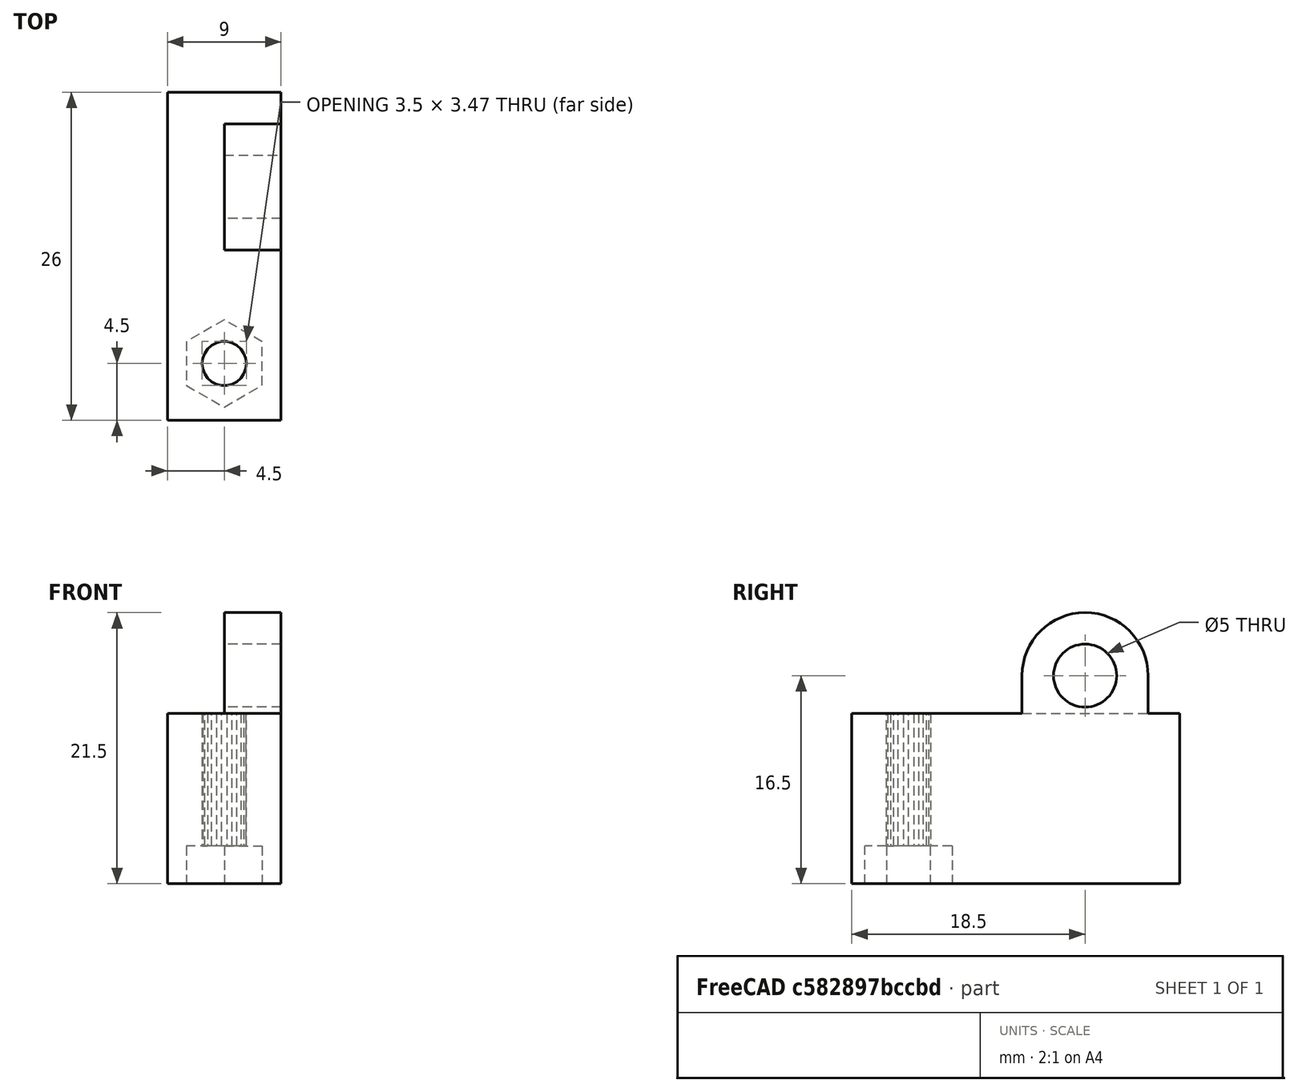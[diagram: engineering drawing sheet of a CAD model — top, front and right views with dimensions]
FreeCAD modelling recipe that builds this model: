
FCSTD DOCUMENT  (FreeCAD 0.22R34198 (Git))
Label: lamp_screw_conductor
License: All rights reserved
LicenseURL: http://en.wikipedia.org/wiki/All_rights_reserved
objects: Mesh::Feature×1, PartDesign::FeatureAdditivePython×1, Sketcher::SketchObject×1, PartDesign::Pad×1, PartDesign::Body×1
note: 7 computed .brp shape members not serialized (recipe doc carries the construction recipe); baked Part::Feature solids carry a one-line shape summary decoded from their .brp

FEATURE [Mesh::Feature] ____________________________________________________  label="Кондуктор гайки светильника"
FEATURE [PartDesign::FeatureAdditivePython] PDW_Add  # link proxy (typed FeaturePython)
  Body = Body
  ClaimChildren = true
  EditPlacementAdjustments = false
  Enabled = 1
  LinkedObject = -> ____________________________________________________
  MeshTolerance = 0.1
  PatternBase = -> ____________________________________________________
  PatternBaseOffset = 0
  PatternBaseScale = 1
  PatternBaseScaleXYZ = (1,1,1)
  PatternOffsetCut = false
  PatternOffsetIntersection = false
  PatternOffsetJoin = 0
  PatternOffsetMode = 0
  PatternOffsetSelfIntersection = false
  PatternOperation = 0
  PatternOperationDefault = None
  PatternScaleCut = false
  PatternShapeOffset = 0
  PatternShapeScale = 1
  PatternShapeScaleXYZ = (1,1,1)
  PatternToolOffset = 0
  PatternToolScale = 1
  PatternToolScaleXYZ = (1,1,1)
  RefineMesh = true
  ShapeManagement = 0
  ShowMeshProps = true
  ShowOffsetProps = false
  ShowScaleProps = false
  ShowWarnings = true
  TipBaseOffset = 0
  TipBaseScale = 1
  TipBaseScaleXYZ = (1,1,1)
  TipOffsetCut = false
  TipOffsetIntersection = false
  TipOffsetJoin = 0
  TipOffsetMode = 0
  TipOffsetSelfIntersection = false
  TipOperation = 0
  TipOperationDefault = Fuse
  TipScaleCut = false
  TipShapeOffset = 0
  TipShapeScale = 1
  TipShapeScaleXYZ = (1,1,1)
  TipTool = -> ____________________________________________________
  TipToolOffset = 0
  TipToolScale = 1
  TipToolScaleXYZ = (1,1,1)
  Type = Additive
  UsePatternBaseAddSubShape = false
  UsePatternToolAddSubShape = false
  UseTipBaseAddSubShape = false
  UseTipToolAddSubShape = false
  Version = 0.2023.08.13
FEATURE [Sketcher::SketchObject] Sketch
  ExternalGeometry = -> [PDW_Add]
  FullyConstrained = false
  MapMode = 5
  Placement = pos=(0,0,0) rot=(0.57735,0.57735,0.57735;2.0944rad)
  Support = -> [YZ_Plane]
  sketch-geometry (6):
    g0: Circle CenterX=18.5 CenterY=16.5 CenterZ=0 NormalX=0 NormalY=0 NormalZ=1 AngleXU=0 Radius=2.5
    g1: LineSegment StartX=13.4979 StartY=13.5 StartZ=0 EndX=13.5 EndY=16.5034 EndZ=0
    g2: LineSegment StartX=23.5 StartY=16.5 StartZ=0 EndX=23.5 EndY=13.5 EndZ=0
    g3: ArcOfCircle CenterX=18.5 CenterY=16.5 CenterZ=0 NormalX=0 NormalY=0 NormalZ=1 AngleXU=0 Radius=5 StartAngle=2.23e-14 EndAngle=3.1409
    g4: GeomPoint X=23.5 Y=14525 Z=0
    g5: LineSegment StartX=13.4979 StartY=13.5 StartZ=0 EndX=23.5 EndY=13.5 EndZ=0
  constraints (14):
    c: Diameter(g0) = 5
    c: PointOnObject(g2,g-3)
    c: PointOnObject(g4,g1)
    c: PointOnObject(g4,g2)
    c: Tangent(g1,g3) = 1.5708
    c: Tangent(g2,g3) = 1.5708
    c: Coincident(g3,g0)
    c: Radius(g3) = 5
    c: Vertical(g2)
    c: DistanceY(g0) = 16.5
    c: DistanceX(g0) = 18.5
    c: PointOnObject(g1,g-3)
    c: Coincident(g5,g1)
    c: Coincident(g5,g2)
FEATURE [PartDesign::Pad] Pad
  BaseFeature = -> PDW_Add
  Direction = (1,-2e-16,3e-16)
  Length = 4.5
  Length2 = 10
  Profile = -> Sketch
  ReferenceAxis = -> Sketch [N_Axis]
  Type = 0
FEATURE [PartDesign::Body] Body
  Group = -> [PDW_Add,____________________________________________________,Sketch,Pad]
  Origin = -> Origin
  Tip = -> Pad
